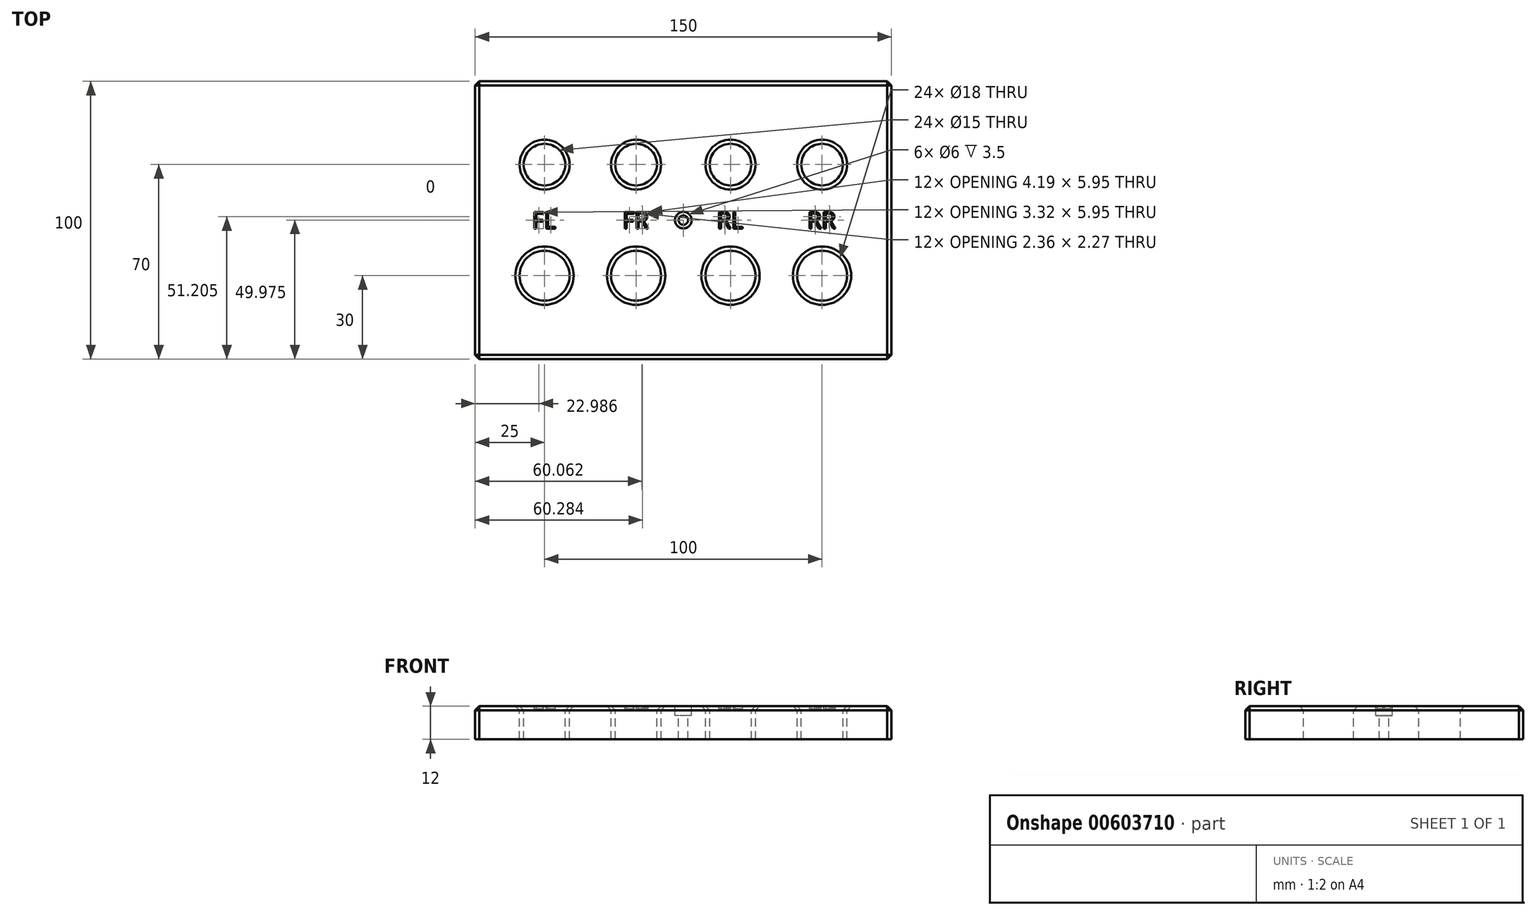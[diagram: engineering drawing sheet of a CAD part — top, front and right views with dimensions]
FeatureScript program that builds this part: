
annotation { "Feature Type Name" : "Feature", "Feature Type Description" : "" }
export const myFeature = defineFeature(function(context is Context, id is Id, definition is map)
    precondition{}
    {
        {
            var Q0;
            Q0=qCreatedBy(makeId("Top.planeOp"),FACE);
            var sketch = newSketch(context, id + "F0", { "sketchPlane" : qUnion([Q0])});
            skLineSegment(sketch, "E0.bottom", {"start": v(75, 50) * mm, "end": v(-75, 50) * mm});
            skLineSegment(sketch, "E0.top", {"start": v(75, -50) * mm, "end": v(-75, -50) * mm});
            skLineSegment(sketch, "E0.left", {"start": v(75, 50) * mm, "end": v(75, -50) * mm});
            skLineSegment(sketch, "E0.right", {"start": v(-75, 50) * mm, "end": v(-75, -50) * mm});
            skPoint(sketch, "E0.middle", {"position": v(0, 0) * mm});
            skLineSegment(sketch, "E1", {"start": v(-75, 20) * mm, "end": v(75, 20) * mm, "construction": true});
            skPoint(sketch, "E2.startSnap0", {"position": v(-75, 0) * mm});
            skPoint(sketch, "E2.endSnap0", {"position": v(75, 0) * mm});
            skCircle(sketch, "E3", {"center": v(-50, 20) * mm, "radius": 7.5 * mm});
            skCircle(sketch, "E4", {"center": v(-17, 20) * mm, "radius": 7.5 * mm});
            skCircle(sketch, "E5", {"center": v(17, 20) * mm, "radius": 7.5 * mm});
            skCircle(sketch, "E6", {"center": v(50, 20) * mm, "radius": 7.5 * mm});
            skLineSegment(sketch, "E7", {"start": v(-75, -20) * mm, "end": v(75, -20) * mm, "construction": true});
            skCircle(sketch, "E8", {"center": v(-50, -20) * mm, "radius": 9 * mm});
            skCircle(sketch, "E9", {"center": v(-17, -20) * mm, "radius": 9 * mm});
            skCircle(sketch, "E10", {"center": v(17, -20) * mm, "radius": 9 * mm});
            skCircle(sketch, "E11", {"center": v(50, -20) * mm, "radius": 9 * mm});
            skPoint(sketch, "E12", {"position": v(-67, -42) * mm});
            skPoint(sketch, "E13", {"position": v(67, -42) * mm});
            skPoint(sketch, "E14", {"position": v(67, 42) * mm});
            skPoint(sketch, "E15", {"position": v(-67, 42) * mm});
            skSolve(sketch);
        }
        {
            var Q0;
            Q0=makeQuery(id+"F0.imprint","IMPRINT",FACE,{"disambiguationData":[TD([[makeQuery(id+"F0.imprint","IMPRINT",EDGE,{"derivedFrom":sQuery(id+"F0.wireOp",EDGE,"E0.bottom")}),1.0]])]});
            extrude(context, id + "F1", {"entities" : qUnion([Q0]), "oppositeDirection" : true, "depth" : 12 * mm, "offsetDistance" : 25 * mm});
        }
        {
            var Q0;
            Q0=makeQuery(id+"F1.opExtrude","SWEPT_EDGE",EDGE,{"disambiguationData":[OSD([sQuery(id+"F0.wireOp",EDGE,"E0.bottom"),sQuery(id+"F0.wireOp",EDGE,"E0.right")])]});
            var Q1;
            Q1=makeQuery(id+"F1.opExtrude","SWEPT_EDGE",EDGE,{"disambiguationData":[OSD([sQuery(id+"F0.wireOp",EDGE,"E0.bottom"),sQuery(id+"F0.wireOp",EDGE,"E0.left")])]});
            var Q2;
            Q2=makeQuery(id+"F1.opExtrude","SWEPT_EDGE",EDGE,{"disambiguationData":[OSD([sQuery(id+"F0.wireOp",EDGE,"E0.top"),sQuery(id+"F0.wireOp",EDGE,"E0.left")])]});
            var Q3;
            Q3=makeQuery(id+"F1.opExtrude","SWEPT_EDGE",EDGE,{"disambiguationData":[OSD([sQuery(id+"F0.wireOp",EDGE,"E0.top"),sQuery(id+"F0.wireOp",EDGE,"E0.right")])]});
            var Q4;
            Q4=makeQuery(id+"F1.opExtrude","CAP_EDGE",EDGE,{"disambiguationData":[OSD([sQuery(id+"F0.wireOp",EDGE,"E0.bottom")])],"isStart":true});
            var Q5;
            Q5=makeQuery(id+"F1.opExtrude","CAP_EDGE",EDGE,{"disambiguationData":[OSD([sQuery(id+"F0.wireOp",EDGE,"E0.top")])],"isStart":true});
            var Q6;
            Q6=makeQuery(id+"F1.opExtrude","CAP_EDGE",EDGE,{"disambiguationData":[OSD([sQuery(id+"F0.wireOp",EDGE,"E0.right")])],"isStart":true});
            var Q7;
            Q7=makeQuery(id+"F1.opExtrude","CAP_EDGE",EDGE,{"disambiguationData":[OSD([sQuery(id+"F0.wireOp",EDGE,"E0.left")])],"isStart":true});
            chamfer(context, id + "F2", {"entities" : qUnion([Q0, Q1, Q2, Q3, Q4, Q5, Q6, Q7]), "width" : 1.5 * mm, "tangentPropagation" : true});
        }
        {
            var Q0;
            Q0=makeQuery(id+"F1.opExtrude","CAP_EDGE",EDGE,{"disambiguationData":[OSD([sQuery(id+"F0.wireOp",EDGE,"E3")])],"isStart":true});
            var Q1;
            Q1=makeQuery(id+"F1.opExtrude","CAP_EDGE",EDGE,{"disambiguationData":[OSD([sQuery(id+"F0.wireOp",EDGE,"E4")])],"isStart":true});
            var Q2;
            Q2=makeQuery(id+"F1.opExtrude","CAP_EDGE",EDGE,{"disambiguationData":[OSD([sQuery(id+"F0.wireOp",EDGE,"E5")])],"isStart":true});
            var Q3;
            Q3=makeQuery(id+"F1.opExtrude","CAP_EDGE",EDGE,{"disambiguationData":[OSD([sQuery(id+"F0.wireOp",EDGE,"E6")])],"isStart":true});
            var Q4;
            Q4=makeQuery(id+"F1.opExtrude","CAP_EDGE",EDGE,{"disambiguationData":[OSD([sQuery(id+"F0.wireOp",EDGE,"E8")])],"isStart":true});
            var Q5;
            Q5=makeQuery(id+"F1.opExtrude","CAP_EDGE",EDGE,{"disambiguationData":[OSD([sQuery(id+"F0.wireOp",EDGE,"E9")])],"isStart":true});
            var Q6;
            Q6=makeQuery(id+"F1.opExtrude","CAP_EDGE",EDGE,{"disambiguationData":[OSD([sQuery(id+"F0.wireOp",EDGE,"E10")])],"isStart":true});
            var Q7;
            Q7=makeQuery(id+"F1.opExtrude","CAP_EDGE",EDGE,{"disambiguationData":[OSD([sQuery(id+"F0.wireOp",EDGE,"E11")])],"isStart":true});
            chamfer(context, id + "F3", {"entities" : qUnion([Q0, Q1, Q2, Q3, Q4, Q5, Q6, Q7]), "width" : 1.5 * mm, "tangentPropagation" : true});
        }
        {
            var Q0;
            Q0=sQuery(id+"F0.wireOp",VERTEX,"E0.middle");
            var Q1;
            Q1=makeQuery(id+"F1.opExtrude","SWEPT_BODY",BODY,{"disambiguationData":[OSD([sQuery(id+"F0.wireOp",EDGE,"E0.bottom"),sQuery(id+"F0.wireOp",EDGE,"E0.top"),sQuery(id+"F0.wireOp",EDGE,"E0.left"),sQuery(id+"F0.wireOp",EDGE,"E0.right"),sQuery(id+"F0.wireOp",EDGE,"E3"),sQuery(id+"F0.wireOp",EDGE,"E4"),sQuery(id+"F0.wireOp",EDGE,"E5"),sQuery(id+"F0.wireOp",EDGE,"E6"),sQuery(id+"F0.wireOp",EDGE,"E8"),sQuery(id+"F0.wireOp",EDGE,"E9"),sQuery(id+"F0.wireOp",EDGE,"E10"),sQuery(id+"F0.wireOp",EDGE,"E11")])]});
            hole(context, id + "F4", {"style" : HoleStyle.C_BORE, "endStyle" : HoleEndStyle.THROUGH, "holeDiameter" : 3.4 * mm, "cBoreDiameter" : 6 * mm, "cBoreDepth" : 3.5 * mm, "majorDiameter" : 5 * mm, "isTappedThrough" : true, "tappedDepth" : 12 * mm, "tapClearance" : 3, "startFromSketch" : true, "locations" : qUnion([Q0]), "scope" : qUnion([Q1])});
        }
        {
            var Q0;
            Q0=qCreatedBy(makeId("Top.planeOp"),FACE);
            var sketch = newSketch(context, id + "F5", { "sketchPlane" : qUnion([Q0])});
            skLineSegment(sketch, "E16", {"start": v(-73.16, 3) * mm, "end": v(73.36, 3) * mm, "construction": true});
            skLineSegment(sketch, "E17", {"start": v(-73.16, -3) * mm, "end": v(73.36, -3) * mm, "construction": true});
            skPoint(sketch, "E18.0", {"position": v(-50, 20) * mm});
            skText(sketch, "E19", { "text": "FL", "fontName": "OpenSans-Regular.ttf"});
            skLineSegment(sketch, "E20", {"start": v(-50, 20) * mm, "end": v(-50, -3) * mm, "construction": true});
            skPoint(sketch, "E21.0", {"position": v(-17, 20) * mm});
            skPoint(sketch, "E22.0", {"position": v(17, 20) * mm});
            skPoint(sketch, "E23.0", {"position": v(50, 20) * mm});
            skLineSegment(sketch, "E24", {"start": v(-17, 20) * mm, "end": v(-17, -3) * mm, "construction": true});
            skLineSegment(sketch, "E25", {"start": v(17, 20) * mm, "end": v(17, -3) * mm, "construction": true});
            skLineSegment(sketch, "E26", {"start": v(50, 20) * mm, "end": v(50, -3) * mm, "construction": true});
            skText(sketch, "E27", { "text": "FR", "fontName": "OpenSans-Regular.ttf"});
            skText(sketch, "E28", { "text": "RL", "fontName": "OpenSans-Regular.ttf"});
            skText(sketch, "E29", { "text": "RR", "fontName": "OpenSans-Regular.ttf"});
            const initialGuessF5  = {"E19": [-0.05449, -0.003, 1, 0, 0.006], "E27": [-0.02193, -0.003, 1, 0, 0.006], "E28": [0.01209, -0.003, 1, 0, 0.006], "E29": [0.04465, -0.003, 1, 0, 0.006]};
            skSetInitialGuess(sketch, initialGuessF5);
            skSolve(sketch);
        }
        {
            var Q0;
            Q0=qSketchRegion(id+"F5",true);
            extrude(context, id + "F6", {"entities" : qUnion([Q0]), "operationType" : NewBodyOperationType.REMOVE, "oppositeDirection" : true, "depth" : 1 * mm, "offsetDistance" : 25 * mm});
        }
    });
